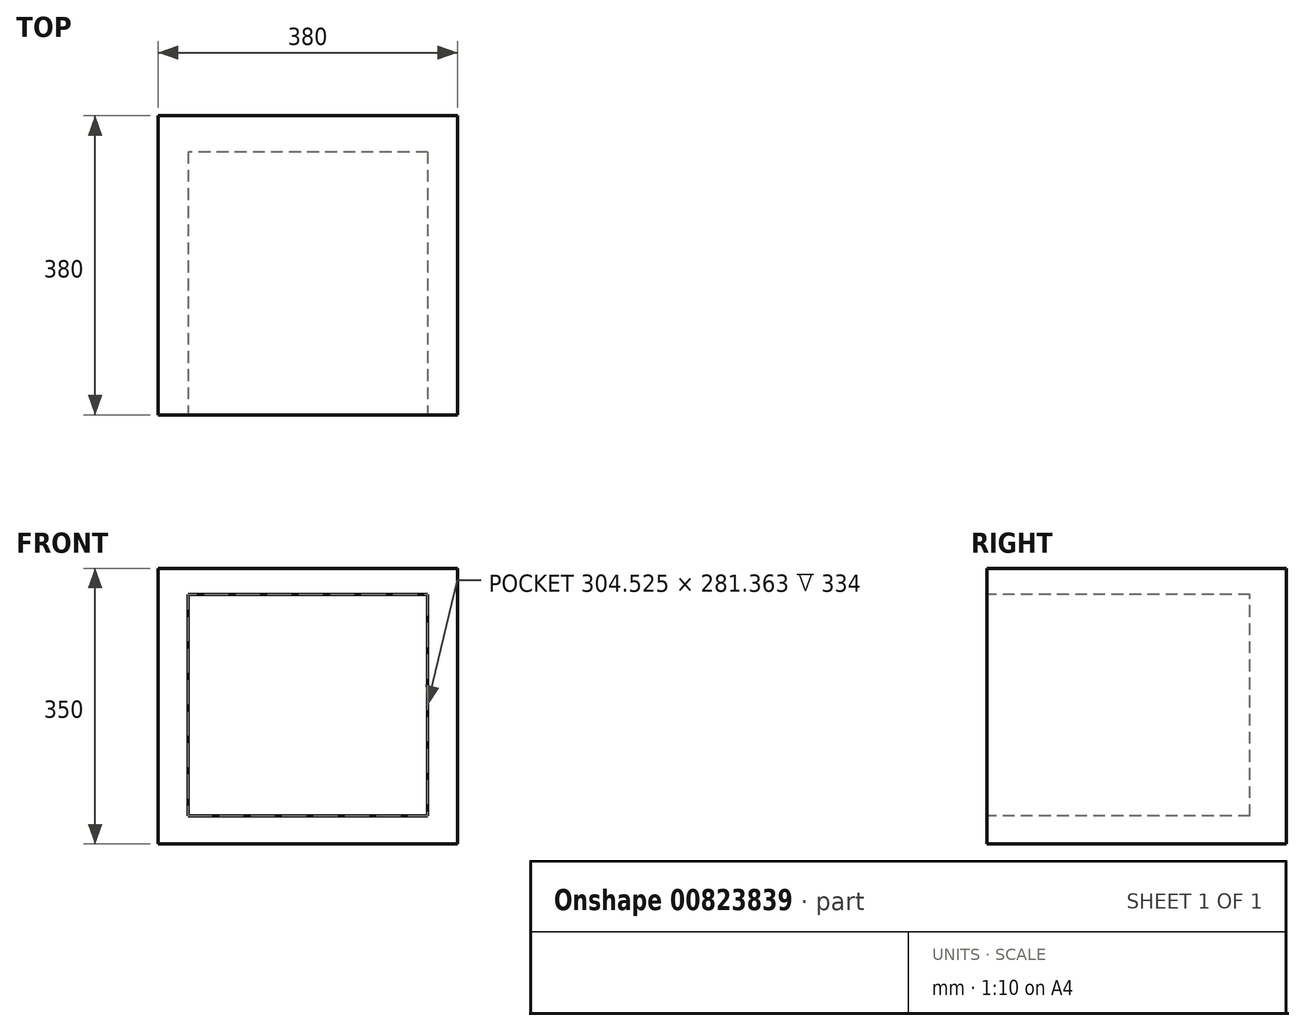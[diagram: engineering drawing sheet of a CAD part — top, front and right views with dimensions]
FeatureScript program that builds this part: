
annotation { "Feature Type Name" : "Feature", "Feature Type Description" : "" }
export const myFeature = defineFeature(function(context is Context, id is Id, definition is map)
    precondition{}
    {
        {
            var Q0;
            Q0=qCreatedBy(makeId("Top.planeOp"),FACE);
            var sketch = newSketch(context, id + "F0", { "sketchPlane" : qUnion([Q0])});
            skLineSegment(sketch, "E0.bottom", {"start": v(190, -190) * mm, "end": v(-190, -190) * mm});
            skLineSegment(sketch, "E0.top", {"start": v(190, 190) * mm, "end": v(-190, 190) * mm});
            skLineSegment(sketch, "E0.left", {"start": v(190, -190) * mm, "end": v(190, 190) * mm});
            skLineSegment(sketch, "E0.right", {"start": v(-190, -190) * mm, "end": v(-190, 190) * mm});
            skPoint(sketch, "E0.middle", {"position": v(0, 0) * mm});
            skSolve(sketch);
        }
        {
            var Q0;
            Q0 = qSketchRegion(id + "F0", true);
            extrude(context, id + "F1", {"entities" : qUnion([Q0]), "depth" : 350 * mm, "offsetDistance" : 25 * mm});
        }
        {
            var Q0;
            Q0=makeQuery(id+"F1.opExtrude","SWEPT_FACE",FACE,{"disambiguationData":[OSD([sQuery(id+"F0.wireOp",EDGE,"E0.bottom")])]});
            var sketch = newSketch(context, id + "F2", { "sketchPlane" : qUnion([Q0])});
            skLineSegment(sketch, "E1.bottom", {"start": v(152.26, 35.25) * mm, "end": v(-152.26, 35.25) * mm});
            skLineSegment(sketch, "E1.top", {"start": v(152.26, 316.61) * mm, "end": v(-152.26, 316.61) * mm});
            skLineSegment(sketch, "E1.left", {"start": v(152.26, 35.25) * mm, "end": v(152.26, 316.61) * mm});
            skLineSegment(sketch, "E1.right", {"start": v(-152.26, 35.25) * mm, "end": v(-152.26, 316.61) * mm});
            skPoint(sketch, "E1.middle", {"position": v(0, 175.93) * mm});
            skSolve(sketch);
        }
        {
            var Q0;
            Q0=makeQuery(id+"F2.imprint","IMPRINT",FACE,{"disambiguationData":[TD([[makeQuery(id+"F2.imprint","IMPRINT",EDGE,{"derivedFrom":sQuery(id+"F2.wireOp",EDGE,"E1.bottom")}),-1.0]])]});
            extrude(context, id + "F3", {"entities" : qUnion([Q0]), "operationType" : NewBodyOperationType.REMOVE, "oppositeDirection" : true, "depth" : 334 * mm, "offsetDistance" : 25 * mm});
        }
    });
